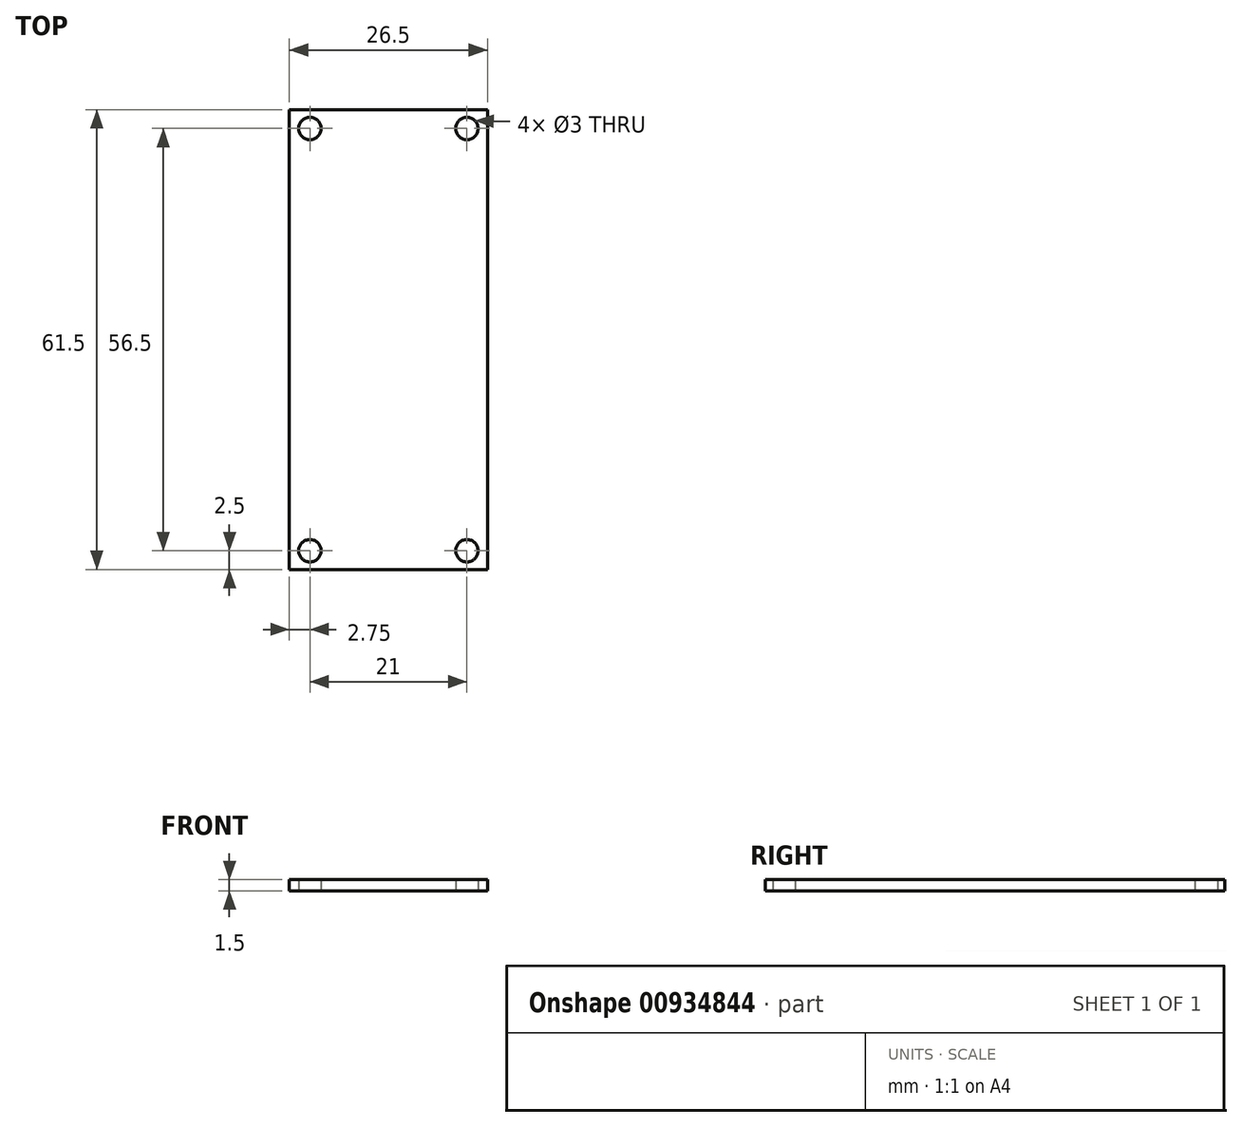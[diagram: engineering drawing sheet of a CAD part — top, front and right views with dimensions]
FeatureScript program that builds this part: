
annotation { "Feature Type Name" : "Feature", "Feature Type Description" : "" }
export const myFeature = defineFeature(function(context is Context, id is Id, definition is map)
    precondition{}
    {
        {
            var Q0;
            Q0=qCreatedBy(makeId("Top.planeOp"),FACE);
            var sketch = newSketch(context, id + "F0", { "sketchPlane" : qUnion([Q0])});
            skLineSegment(sketch, "E0.bottom", {"start": v(13.25, -30.75) * mm, "end": v(-13.25, -30.75) * mm});
            skLineSegment(sketch, "E0.top", {"start": v(13.25, 30.75) * mm, "end": v(-13.25, 30.75) * mm});
            skLineSegment(sketch, "E0.left", {"start": v(13.25, -30.75) * mm, "end": v(13.25, 30.75) * mm});
            skLineSegment(sketch, "E0.right", {"start": v(-13.25, -30.75) * mm, "end": v(-13.25, 30.75) * mm});
            skPoint(sketch, "E1.middle", {"position": v(0, 0) * mm});
            skCircle(sketch, "E2", {"center": v(10.5, 28.25) * mm, "radius": 1.5 * mm});
            skCircle(sketch, "E3", {"center": v(10.5, -28.25) * mm, "radius": 1.5 * mm});
            skCircle(sketch, "E4", {"center": v(-10.5, -28.25) * mm, "radius": 1.5 * mm});
            skCircle(sketch, "E5", {"center": v(-10.5, 28.25) * mm, "radius": 1.5 * mm});
            skLineSegment(sketch, "E6.bottom", {"start": v(10.5, -28.25) * mm, "end": v(-10.5, -28.25) * mm, "construction": true});
            skLineSegment(sketch, "E6.top", {"start": v(10.5, 28.25) * mm, "end": v(-10.5, 28.25) * mm, "construction": true});
            skLineSegment(sketch, "E6.left", {"start": v(10.5, -28.25) * mm, "end": v(10.5, 28.25) * mm, "construction": true});
            skLineSegment(sketch, "E6.right", {"start": v(-10.5, -28.25) * mm, "end": v(-10.5, 28.25) * mm, "construction": true});
            skSolve(sketch);
        }
        {
            var Q0;
            Q0=qSketchRegion(id+"F0",true);
            extrude(context, id + "F1", {"entities" : qUnion([Q0]), "depth" : 1.5 * mm, "offsetDistance" : 25 * mm});
        }
    });
